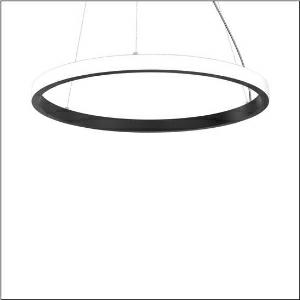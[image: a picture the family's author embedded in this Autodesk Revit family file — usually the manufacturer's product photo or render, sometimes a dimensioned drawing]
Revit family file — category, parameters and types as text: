
# Revit family: silica_r__21_ring-o_5pjbo4d3104a_8b26
name_source: partatom
category: Lighting Fixtures
units: mm (PartAtom-declared; Revit-internal decimal feet)

## family parameters
Cut with Voids When Loaded = No
Host = Face
Light Source = No
Part Type = Normal
Room Calculation Point = No
Round Connector Dimension = Use Diameter
Shared = No

## types (1)
- Silica® 21 Ring-O (1 x LED, 9260 lm, 140 W, 4000K)
    Apparent Load = 140 VA
    CIE Flux Codes = 2 16 49 50 100
    Color Rendering = 80
    Color Temperature = 4000K
    Default Elevation = 1800 mm
    Description = Silica® 21 Ring-O, suspended luminaire, of PMMA, frosted, light emission: outer ring side luminous distribution, primary light characteristic: symmetric, installation type: suspended mounting, LED, rated luminous flux: 9.260lm, luminous efficacy: 66lm/W, light colour: 840, colour temperature: 4000K, control gear: DALI 2, with terminal, 5-pole, mains connection: 230V, AC/DC, 0/50..60Hz, rated input power: 140W, housing, of extruded aluminium section, jet black (RAL 9005), diameter: 1.480mm, ceiling canopy, jet black (RAL 9005), protection rating (lamp compartment): IP40, insulation class (complete): insulation class I (protective earthing), certification: CE, impact resistance: IK02, permissible operating ambient temperature: 0..+35°C, packaging unit: 1 piece
    Height = 48 mm  [stored 0.15748 ft]
    Lamp = 1 x LED
    Lamp Light Flux = 9260 lm
    Lamp Power = 140 W
    Lamp count = 1
    Length = 1480 mm
    Luminous efficacy = 66 lm/W
    Manufacturer = Siteco
    ModVariant = No
    Model = 5PJBO4D3104A
    Mounting Place = Ceiling
    Mounting Type = Pendant
    Number of Poles = 1
    OnlyDefault = Yes
    Power Factor = 1
    Product Name = Silica® 21 Ring-O
    Product group = suspended luminaire
    ProductGroupID = 905
    Protection Class = Protection class I
    Protection Degree = IP 40
    RLX_Detail_Level = 1
    RLX_Emergency_Light_Flux = 0 lm
    RLX_Emergency_Type = 0
    RLX_Emergency_Type_DB = No
    RlxData = <blob elided: 20565 chars, md5=7eebd440>
    Socket = socket
    Standby Power = 0 W
    System Light Flux = 9260 lm
    System Power = 140 W
    Type Comments = Product without accessories
    Type Image = l_1258389.jpg
    URL = http://relux.com
    VarID = ---
    Voltage = 0 V
    Weight = 0.00 kg
    Width = 0 mm  [stored 0 ft]

note: [stored X ft] marks values corroborated as IEEE doubles in the binary element streams (Revit-internal decimal feet)

## geometry (parser evidence)
native form markers: Blend x4, Sweep x14
no freeform markers — native parametric forms only
